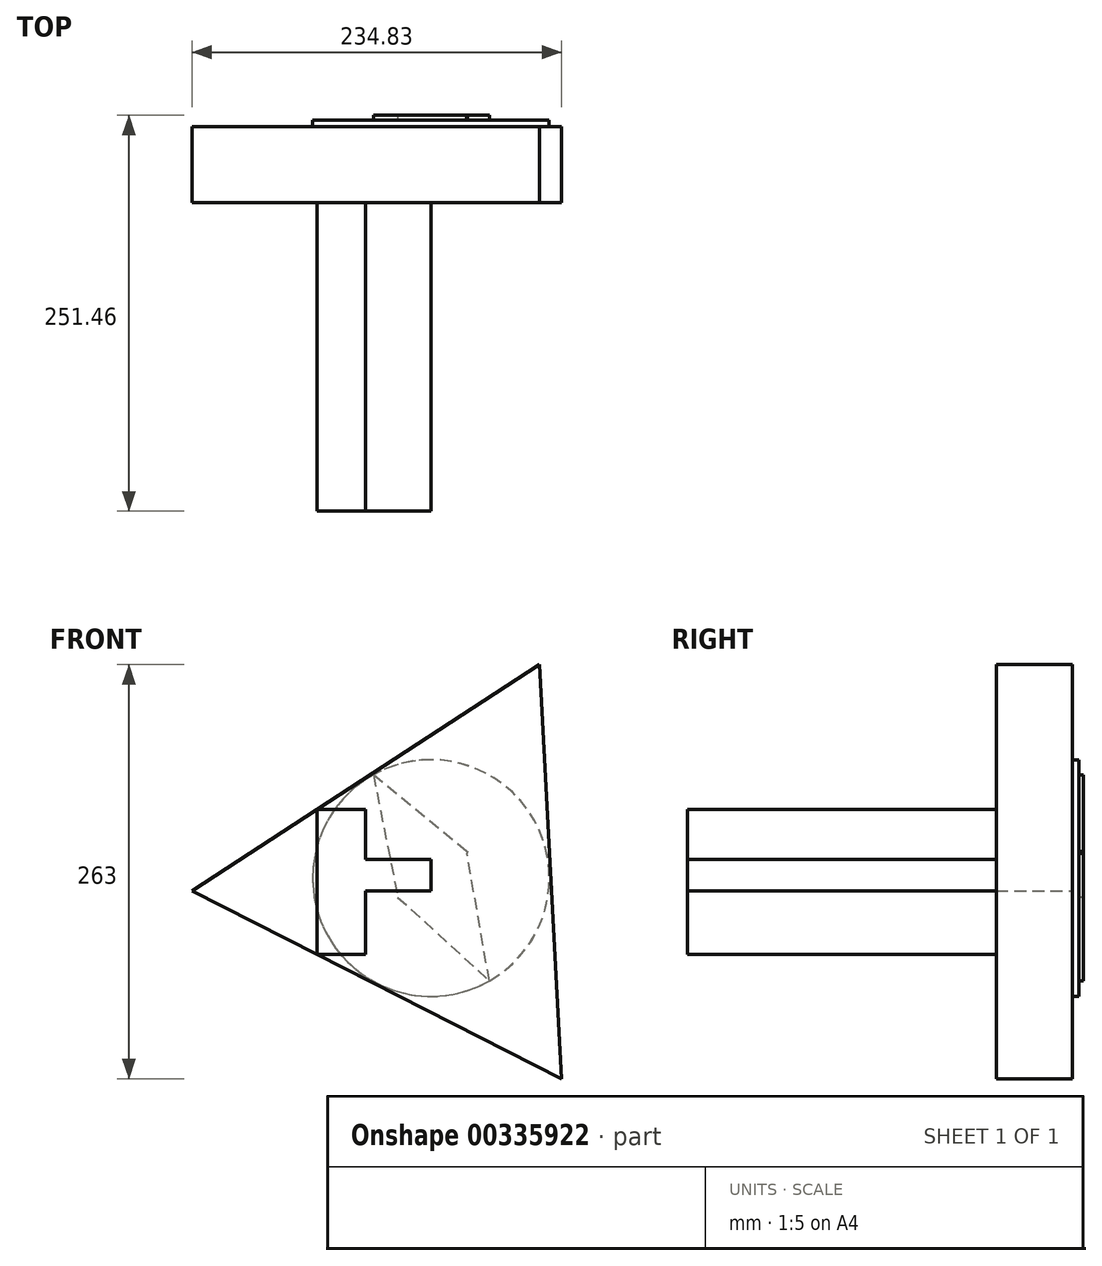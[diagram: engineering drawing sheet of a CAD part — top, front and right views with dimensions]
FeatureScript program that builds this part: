
annotation { "Feature Type Name" : "Feature", "Feature Type Description" : "" }
export const myFeature = defineFeature(function(context is Context, id is Id, definition is map)
    precondition{}
    {
        {
            var Q0;
            Q0=qCreatedBy(makeId("Front.planeOp"),FACE);
            var sketch = newSketch(context, id + "F0", { "sketchPlane" : qUnion([Q0])});
            skCircle(sketch, "E0", {"center": v(0, 0) * mm, "radius": 76.03 * mm});
            skCircle(sketch, "E1.cCircle", {"center": v(0, 0) * mm, "radius": 76.03 * mm, "construction": true});
            skLineSegment(sketch, "E1.0", {"start": v(-151.84, -8.16) * mm, "end": v(68.85, 135.58) * mm});
            skLineSegment(sketch, "E1.1", {"start": v(68.85, 135.58) * mm, "end": v(82.99, -127.42) * mm});
            skLineSegment(sketch, "E1.2", {"start": v(82.99, -127.42) * mm, "end": v(-151.84, -8.16) * mm});
            skPoint(sketch, "E1.0.midPoint", {"position": v(-41.5, 63.7) * mm});
            skSolve(sketch);
        }
        {
            var Q0;
            {var subQ0=sQuery(id+"F0.wireOp",EDGE,"E0");var subQ1=makeQuery(id+"F0.imprint","INTERSECT",VERTEX,{"derivedFrom":[subQ0,sQuery(id+"F0.wireOp",EDGE,"E1.0")]});Q0=makeQuery(id+"F0.imprint","IMPRINT",FACE,{"disambiguationData":[TD([[makeQuery(id+"F0.imprint","IMPRINT",EDGE,{"disambiguationData":[TD([[subQ1,1.0]])],"derivedFrom":subQ0}),1.0]])]});}
            var Q1;
            {var subQ0=sQuery(id+"F0.wireOp",EDGE,"E1.0");var subQ1=sQuery(id+"F0.wireOp",EDGE,"E0");var subQ2=makeQuery(id+"F0.imprint","INTERSECT",VERTEX,{"derivedFrom":[subQ1,subQ0]});Q1=makeQuery(id+"F0.imprint","IMPRINT",FACE,{"disambiguationData":[TD([[makeQuery(id+"F0.imprint","IMPRINT",EDGE,{"disambiguationData":[TD([[subQ2,-1.0]])],"derivedFrom":subQ1}),-1.0]])]});}
            var Q2;
            {var subQ0=sQuery(id+"F0.wireOp",EDGE,"E1.0");var subQ1=sQuery(id+"F0.wireOp",EDGE,"E0");var subQ2=makeQuery(id+"F0.imprint","INTERSECT",VERTEX,{"derivedFrom":[subQ1,subQ0]});Q2=makeQuery(id+"F0.imprint","IMPRINT",FACE,{"disambiguationData":[TD([[makeQuery(id+"F0.imprint","IMPRINT",EDGE,{"disambiguationData":[TD([[subQ2,1.0]])],"derivedFrom":subQ1}),-1.0]])]});}
            var Q3;
            {var subQ0=sQuery(id+"F0.wireOp",EDGE,"E1.1");var subQ1=sQuery(id+"F0.wireOp",EDGE,"E0");var subQ2=makeQuery(id+"F0.imprint","INTERSECT",VERTEX,{"derivedFrom":[subQ1,subQ0]});Q3=makeQuery(id+"F0.imprint","IMPRINT",FACE,{"disambiguationData":[TD([[makeQuery(id+"F0.imprint","IMPRINT",EDGE,{"disambiguationData":[TD([[subQ2,1.0]])],"derivedFrom":subQ1}),-1.0]])]});}
            extrude(context, id + "F1", {"entities" : qUnion([Q0, Q1, Q2, Q3]), "depth" : 48.26 * mm});
        }
        {
            var Q0;
            Q0=makeQuery(id+"F1.opExtrude","CAP_FACE",FACE,{"disambiguationData":[OSD([sQuery(id+"F0.wireOp",EDGE,"E1.0"),sQuery(id+"F0.wireOp",EDGE,"E1.1"),sQuery(id+"F0.wireOp",EDGE,"E1.2")])],"isStart":true});
            var sketch = newSketch(context, id + "F2", { "sketchPlane" : qUnion([Q0])});
            skCircle(sketch, "E2", {"center": v(0, 0) * mm, "radius": 75.13 * mm});
            skSolve(sketch);
        }
        {
            var Q0;
            Q0=makeQuery(id+"F2.imprint","IMPRINT",FACE,{"disambiguationData":[TD([[makeQuery(id+"F2.imprint","IMPRINT",EDGE,{"derivedFrom":sQuery(id+"F2.wireOp",EDGE,"E2")}),1.0]])]});
            extrude(context, id + "F3", {"entities" : qUnion([Q0]), "operationType" : NewBodyOperationType.ADD, "depth" : 4.06 * mm});
        }
        {
            var Q0;
            Q0=makeQuery(id+"F3.opExtrude","CAP_FACE",FACE,{"disambiguationData":[OSD([sQuery(id+"F2.wireOp",EDGE,"E2")])],"isStart":false});
            var sketch = newSketch(context, id + "F4", { "sketchPlane" : qUnion([Q0])});
            skLineSegment(sketch, "E3", {"start": v(36.58, 65.62) * mm, "end": v(21.11, -12.15) * mm});
            skLineSegment(sketch, "E4", {"start": v(21.11, -12.15) * mm, "end": v(-37.07, -65.34) * mm});
            skLineSegment(sketch, "E5", {"start": v(-37.07, -65.34) * mm, "end": v(-22.67, 16.94) * mm});
            skLineSegment(sketch, "E6", {"start": v(-22.67, 16.94) * mm, "end": v(36.58, 65.62) * mm});
            skSolve(sketch);
        }
        {
            var Q0;
            Q0=makeQuery(id+"F4.imprint","IMPRINT",FACE,{"disambiguationData":[TD([[makeQuery(id+"F4.imprint","IMPRINT",EDGE,{"derivedFrom":sQuery(id+"F4.wireOp",EDGE,"E3")}),-1.0]])]});
            var sketch = newSketch(context, id + "F5", { "sketchPlane" : qUnion([Q0])});
            skLineSegment(sketch, "E7", {"start": v(21.11, -11.42) * mm, "end": v(12.05, 16.76) * mm});
            skLineSegment(sketch, "E8", {"start": v(12.05, 16.76) * mm, "end": v(-23.22, 16.76) * mm});
            skLineSegment(sketch, "E9", {"start": v(-23.22, 16.76) * mm, "end": v(-11.72, -16.53) * mm});
            skLineSegment(sketch, "E10", {"start": v(-11.72, -16.53) * mm, "end": v(21.11, -11.42) * mm});
            skSolve(sketch);
        }
        {
            var Q0;
            Q0=makeQuery(id+"F4.imprint","IMPRINT",FACE,{"disambiguationData":[TD([[makeQuery(id+"F4.imprint","IMPRINT",EDGE,{"derivedFrom":sQuery(id+"F4.wireOp",EDGE,"E3")}),-1.0]])]});
            var Q1;
            Q1 = qSketchRegion(id + "F5", true);
            extrude(context, id + "F6", {"entities" : qUnion([Q0, Q1]), "operationType" : NewBodyOperationType.ADD, "depth" : 1.52 * mm});
        }
        {
            var Q0;
            Q0 = qSketchRegion(id + "F5", true);
            var Q1;
            Q1=makeQuery(id+"F6.boolean.opBoolean","MERGE",FACE,{"derivedFrom":[makeQuery(id+"F6.opExtrude","CAP_FACE",FACE,{"disambiguationData":[OSD([sQuery(id+"F4.wireOp",EDGE,"E3"),sQuery(id+"F4.wireOp",EDGE,"E4"),sQuery(id+"F4.wireOp",EDGE,"E5"),sQuery(id+"F4.wireOp",EDGE,"E6")])],"isStart":false}),makeQuery(id+"F6.opExtrude","CAP_FACE",FACE,{"disambiguationData":[OSD([sQuery(id+"F5.wireOp",EDGE,"E7"),sQuery(id+"F5.wireOp",EDGE,"E8"),sQuery(id+"F5.wireOp",EDGE,"E9"),sQuery(id+"F5.wireOp",EDGE,"E10")])],"isStart":false})]});
            extrude(context, id + "F7", {"entities" : qUnion([Q0, Q1]), "operationType" : NewBodyOperationType.ADD, "depth" : 1.52 * mm});
        }
        {
            var Q0;
            Q0=makeQuery(id+"F1.opExtrude","CAP_FACE",FACE,{"disambiguationData":[OSD([sQuery(id+"F0.wireOp",EDGE,"E1.0"),sQuery(id+"F0.wireOp",EDGE,"E1.1"),sQuery(id+"F0.wireOp",EDGE,"E1.2")])],"isStart":false});
            var sketch = newSketch(context, id + "F8", { "sketchPlane" : qUnion([Q0])});
            skLineSegment(sketch, "E11", {"start": v(-72.44, -48.48) * mm, "end": v(-72.44, 43.55) * mm});
            skLineSegment(sketch, "E12", {"start": v(-72.44, 43.55) * mm, "end": v(-41.5, 43.55) * mm});
            skPoint(sketch, "E12.endSnap0", {"position": v(-41.5, 63.7) * mm});
            skLineSegment(sketch, "E13", {"start": v(-41.5, 43.55) * mm, "end": v(-41.5, 11.8) * mm});
            skLineSegment(sketch, "E14", {"start": v(-41.5, 11.8) * mm, "end": v(0, 11.8) * mm});
            skLineSegment(sketch, "E15", {"start": v(0, 11.8) * mm, "end": v(0, -8.16) * mm});
            skLineSegment(sketch, "E16", {"start": v(0, -8.16) * mm, "end": v(-41.5, -8.16) * mm});
            skLineSegment(sketch, "E17", {"start": v(-41.5, -8.16) * mm, "end": v(-41.5, -48.5) * mm});
            skLineSegment(sketch, "E18", {"start": v(-41.5, -48.5) * mm, "end": v(-72.44, -48.48) * mm});
            skSolve(sketch);
        }
        {
            var Q0;
            Q0 = qSketchRegion(id + "F8", true);
            extrude(context, id + "F9", {"entities" : qUnion([Q0]), "operationType" : NewBodyOperationType.ADD, "depth" : 196.1 * mm});
        }
    });
